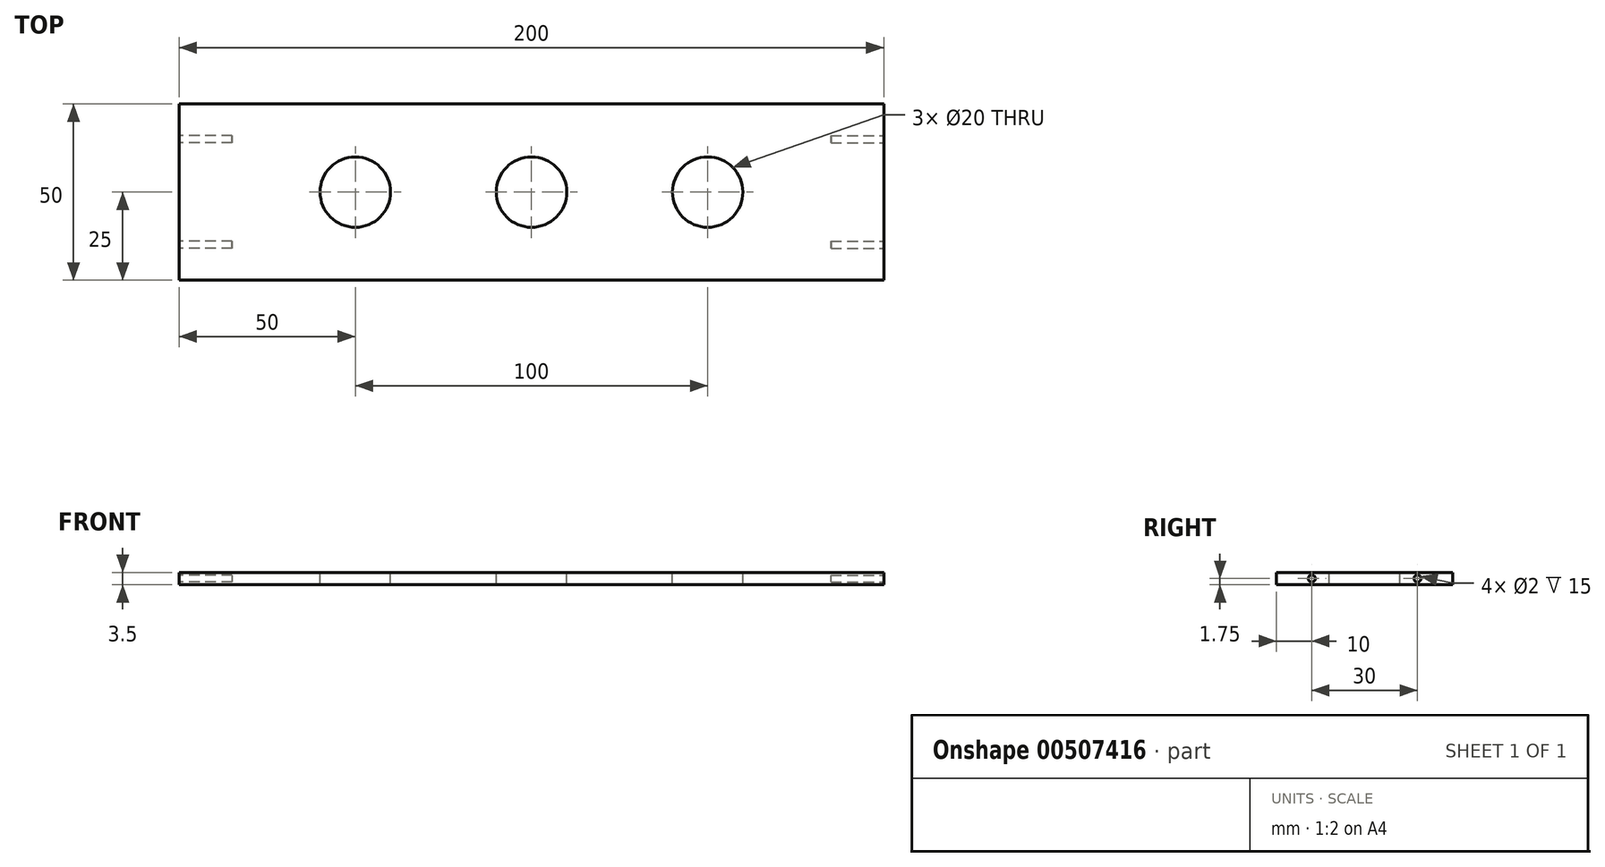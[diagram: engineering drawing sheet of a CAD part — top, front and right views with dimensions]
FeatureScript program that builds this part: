
annotation { "Feature Type Name" : "Feature", "Feature Type Description" : "" }
export const myFeature = defineFeature(function(context is Context, id is Id, definition is map)
    precondition{}
    {
        {
            var Q0;
            Q0=qCreatedBy(makeId("Top.planeOp"),FACE);
            var sketch = newSketch(context, id + "F0", { "sketchPlane" : qUnion([Q0])});
            skLineSegment(sketch, "E0.bottom", {"start": v(100, 25) * mm, "end": v(-100, 25) * mm});
            skLineSegment(sketch, "E0.top", {"start": v(100, -25) * mm, "end": v(-100, -25) * mm});
            skLineSegment(sketch, "E0.left", {"start": v(100, 25) * mm, "end": v(100, -25) * mm});
            skLineSegment(sketch, "E0.right", {"start": v(-100, 25) * mm, "end": v(-100, -25) * mm});
            skPoint(sketch, "E0.middle", {"position": v(0, 0) * mm});
            skSolve(sketch);
        }
        {
            var Q0;
            Q0=makeQuery(id+"F0.imprint","IMPRINT",FACE,{"disambiguationData":[TD([[makeQuery(id+"F0.imprint","IMPRINT",EDGE,{"derivedFrom":sQuery(id+"F0.wireOp",EDGE,"E0.bottom")}),1.0]])]});
            extrude(context, id + "F1", {"entities" : qUnion([Q0]), "endBound" : BoundingType.SYMMETRIC, "depth" : 3.5 * mm});
        }
        {
            var Q0;
            Q0=makeQuery(id+"F1.opExtrude","CAP_FACE",FACE,{"disambiguationData":[OSD([sQuery(id+"F0.wireOp",EDGE,"E0.bottom"),sQuery(id+"F0.wireOp",EDGE,"E0.top"),sQuery(id+"F0.wireOp",EDGE,"E0.left"),sQuery(id+"F0.wireOp",EDGE,"E0.right")])],"isStart":false});
            var sketch = newSketch(context, id + "F2", { "sketchPlane" : qUnion([Q0])});
            skCircle(sketch, "E1", {"center": v(0, 0) * mm, "radius": 10 * mm});
            skCircle(sketch, "E2", {"center": v(50, 0) * mm, "radius": 10 * mm});
            skCircle(sketch, "E3", {"center": v(-50, 0) * mm, "radius": 10 * mm});
            skSolve(sketch);
        }
        {
            var Q0;
            Q0=makeQuery(id+"F2.imprint","IMPRINT",FACE,{"disambiguationData":[TD([[makeQuery(id+"F2.imprint","IMPRINT",EDGE,{"derivedFrom":sQuery(id+"F2.wireOp",EDGE,"E3")}),1.0]])]});
            var Q1;
            Q1=makeQuery(id+"F2.imprint","IMPRINT",FACE,{"disambiguationData":[TD([[makeQuery(id+"F2.imprint","IMPRINT",EDGE,{"derivedFrom":sQuery(id+"F2.wireOp",EDGE,"E1")}),1.0]])]});
            var Q2;
            Q2=makeQuery(id+"F2.imprint","IMPRINT",FACE,{"disambiguationData":[TD([[makeQuery(id+"F2.imprint","IMPRINT",EDGE,{"derivedFrom":sQuery(id+"F2.wireOp",EDGE,"E2")}),1.0]])]});
            extrude(context, id + "F3", {"entities" : qUnion([Q0, Q1, Q2]), "operationType" : NewBodyOperationType.REMOVE, "endBound" : BoundingType.UP_TO_NEXT, "oppositeDirection" : true, "depth" : 25 * mm});
        }
        {
            var Q0;
            Q0=makeQuery(id+"F1.opExtrude","SWEPT_FACE",FACE,{"disambiguationData":[OSD([sQuery(id+"F0.wireOp",EDGE,"E0.left")])]});
            var sketch = newSketch(context, id + "F4", { "sketchPlane" : qUnion([Q0])});
            skCircle(sketch, "E4", {"center": v(-15, 0) * mm, "radius": 1 * mm});
            skCircle(sketch, "E5", {"center": v(15, 0) * mm, "radius": 1 * mm});
            skSolve(sketch);
        }
        {
            var Q0;
            Q0=makeQuery(id+"F4.imprint","IMPRINT",FACE,{"disambiguationData":[TD([[makeQuery(id+"F4.imprint","IMPRINT",EDGE,{"derivedFrom":sQuery(id+"F4.wireOp",EDGE,"E4")}),1.0]])]});
            var Q1;
            Q1=makeQuery(id+"F4.imprint","IMPRINT",FACE,{"disambiguationData":[TD([[makeQuery(id+"F4.imprint","IMPRINT",EDGE,{"derivedFrom":sQuery(id+"F4.wireOp",EDGE,"E5")}),1.0]])]});
            extrude(context, id + "F5", {"entities" : qUnion([Q0, Q1]), "operationType" : NewBodyOperationType.REMOVE, "oppositeDirection" : true, "depth" : 15 * mm});
        }
        {
            var Q0;
            Q0=makeQuery(id+"F1.opExtrude","SWEPT_FACE",FACE,{"disambiguationData":[OSD([sQuery(id+"F0.wireOp",EDGE,"E0.right")])]});
            var sketch = newSketch(context, id + "F6", { "sketchPlane" : qUnion([Q0])});
            skCircle(sketch, "E6", {"center": v(-15, 0) * mm, "radius": 1 * mm});
            skCircle(sketch, "E7", {"center": v(15, 0) * mm, "radius": 1 * mm});
            skSolve(sketch);
        }
        {
            var Q0;
            Q0=makeQuery(id+"F6.imprint","IMPRINT",FACE,{"disambiguationData":[TD([[makeQuery(id+"F6.imprint","IMPRINT",EDGE,{"derivedFrom":sQuery(id+"F6.wireOp",EDGE,"E6")}),1.0]])]});
            var Q1;
            Q1=makeQuery(id+"F6.imprint","IMPRINT",FACE,{"disambiguationData":[TD([[makeQuery(id+"F6.imprint","IMPRINT",EDGE,{"derivedFrom":sQuery(id+"F6.wireOp",EDGE,"E7")}),1.0]])]});
            extrude(context, id + "F7", {"entities" : qUnion([Q0, Q1]), "operationType" : NewBodyOperationType.REMOVE, "oppositeDirection" : true, "depth" : 15 * mm});
        }
    });
